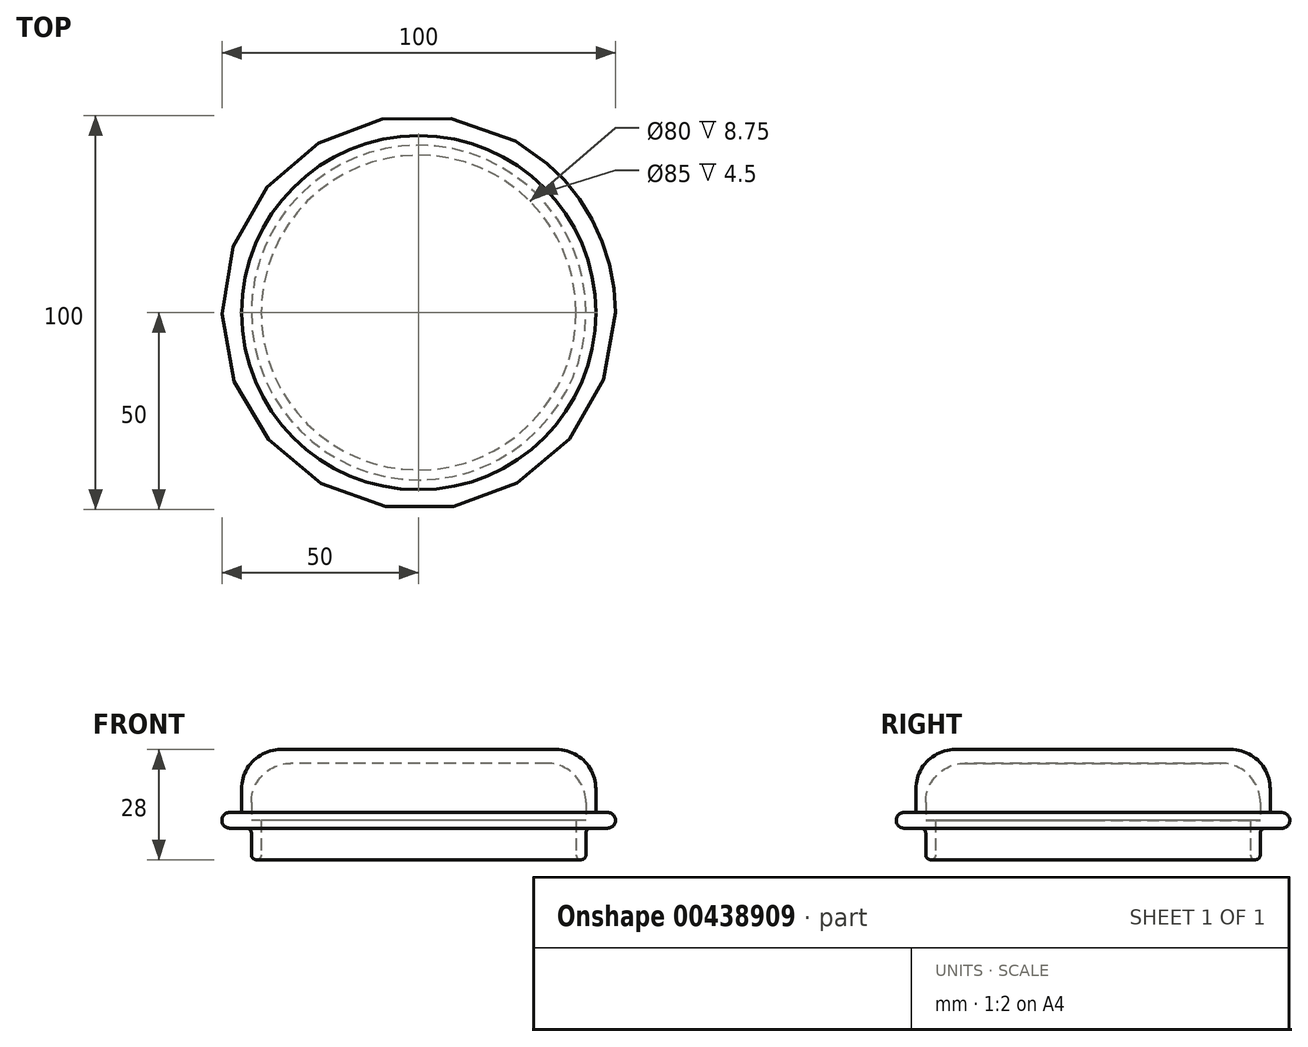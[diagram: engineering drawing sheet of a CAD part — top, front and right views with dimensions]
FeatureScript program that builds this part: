
annotation { "Feature Type Name" : "Feature", "Feature Type Description" : "" }
export const myFeature = defineFeature(function(context is Context, id is Id, definition is map)
    precondition{}
    {
        {
            var Q0;
            Q0=qCreatedBy(makeId("Top.planeOp"),FACE);
            var sketch = newSketch(context, id + "F0", { "sketchPlane" : qUnion([Q0])});
            skCircle(sketch, "E0", {"center": v(0, 0) * mm, "radius": 42.5 * mm});
            skCircle(sketch, "E1", {"center": v(0, 0) * mm, "radius": 45 * mm});
            skCircle(sketch, "E2", {"center": v(0, 0) * mm, "radius": 50 * mm});
            skCircle(sketch, "E3", {"center": v(0, 0) * mm, "radius": 40 * mm});
            skSolve(sketch);
        }
        {
            var Q0;
            Q0=makeQuery(id+"F0.imprint","IMPRINT",FACE,{"disambiguationData":[TD([[makeQuery(id+"F0.imprint","IMPRINT",EDGE,{"derivedFrom":sQuery(id+"F0.wireOp",EDGE,"E0")}),-1.0]])]});
            extrude(context, id + "F1", {"entities" : qUnion([Q0]), "depth" : 20 * mm});
        }
        {
            var Q0;
            Q0=makeQuery(id+"F0.imprint","IMPRINT",FACE,{"disambiguationData":[TD([[makeQuery(id+"F0.imprint","IMPRINT",EDGE,{"derivedFrom":sQuery(id+"F0.wireOp",EDGE,"E1")}),-1.0]])]});
            extrude(context, id + "F2", {"entities" : qUnion([Q0]), "operationType" : NewBodyOperationType.ADD, "depth" : 4 * mm});
        }
        {
            var Q0;
            Q0=makeQuery(id+"F1.opExtrude","CAP_FACE",FACE,{"disambiguationData":[OSD([sQuery(id+"F0.wireOp",EDGE,"E0"),sQuery(id+"F0.wireOp",EDGE,"E1")])],"isStart":false});
            var sketch = newSketch(context, id + "F3", { "sketchPlane" : qUnion([Q0])});
            skCircle(sketch, "E4", {"center": v(0, 0) * mm, "radius": 42.5 * mm});
            skSolve(sketch);
        }
        {
            var Q0;
            Q0 = qSketchRegion(id + "F3", true);
            extrude(context, id + "F4", {"entities" : qUnion([Q0]), "operationType" : NewBodyOperationType.ADD, "oppositeDirection" : true, "depth" : 3.5 * mm});
        }
        {
            var Q0;
            Q0=makeQuery(id+"F0.imprint","IMPRINT",FACE,{"disambiguationData":[TD([[makeQuery(id+"F0.imprint","IMPRINT",EDGE,{"derivedFrom":sQuery(id+"F0.wireOp",EDGE,"E0")}),1.0]])]});
            extrude(context, id + "F5", {"entities" : qUnion([Q0]), "operationType" : NewBodyOperationType.ADD, "depth" : 2 * mm, "hasSecondDirection" : true, "secondDirectionOppositeDirection" : true, "secondDirectionDepth" : 8 * mm});
        }
        {
            var Q0;
            Q0=makeQuery(id+"F4.opExtrude","CAP_FACE",FACE,{"disambiguationData":[OSD([sQuery(id+"F3.wireOp",EDGE,"E4")])],"isStart":false});
            var Q1;
            Q1=makeQuery(id+"F4.boolean.opBoolean","MERGE",FACE,{"derivedFrom":[makeQuery(id+"F1.opExtrude","CAP_FACE",FACE,{"disambiguationData":[OSD([sQuery(id+"F0.wireOp",EDGE,"E0"),sQuery(id+"F0.wireOp",EDGE,"E1")])],"isStart":false}),makeQuery(id+"F4.opExtrude","CAP_FACE",FACE,{"disambiguationData":[OSD([sQuery(id+"F3.wireOp",EDGE,"E4")])],"isStart":true})]});
            fillet(context, id + "F6", {"entities" : qUnion([Q0, Q1]), "radius" : 10 * mm, "tangentPropagation" : true, "allowEdgeOverflow" : false});
        }
        {
            var Q0;
            Q0=makeQuery(id+"F2.opExtrude","SWEPT_FACE",FACE,{"disambiguationData":[OSD([sQuery(id+"F0.wireOp",EDGE,"E2")])]});
            fillet(context, id + "F7", {"entities" : qUnion([Q0]), "radius" : 2 * mm, "tangentPropagation" : true, "allowEdgeOverflow" : false});
        }
        {
            var Q0;
            Q0=makeQuery(id+"F5.opExtrude","CAP_FACE",FACE,{"disambiguationData":[OSD([sQuery(id+"F0.wireOp",EDGE,"E0"),sQuery(id+"F0.wireOp",EDGE,"E3")])],"isStart":true});
            var Q1;
            Q1=makeQuery(id+"F5.opExtrude","SWEPT_FACE",FACE,{"disambiguationData":[OSD([sQuery(id+"F0.wireOp",EDGE,"E0")])]});
            fillet(context, id + "F8", {"entities" : qUnion([Q0, Q1]), "radius" : 1.25 * mm, "tangentPropagation" : true, "allowEdgeOverflow" : false});
        }
    });
